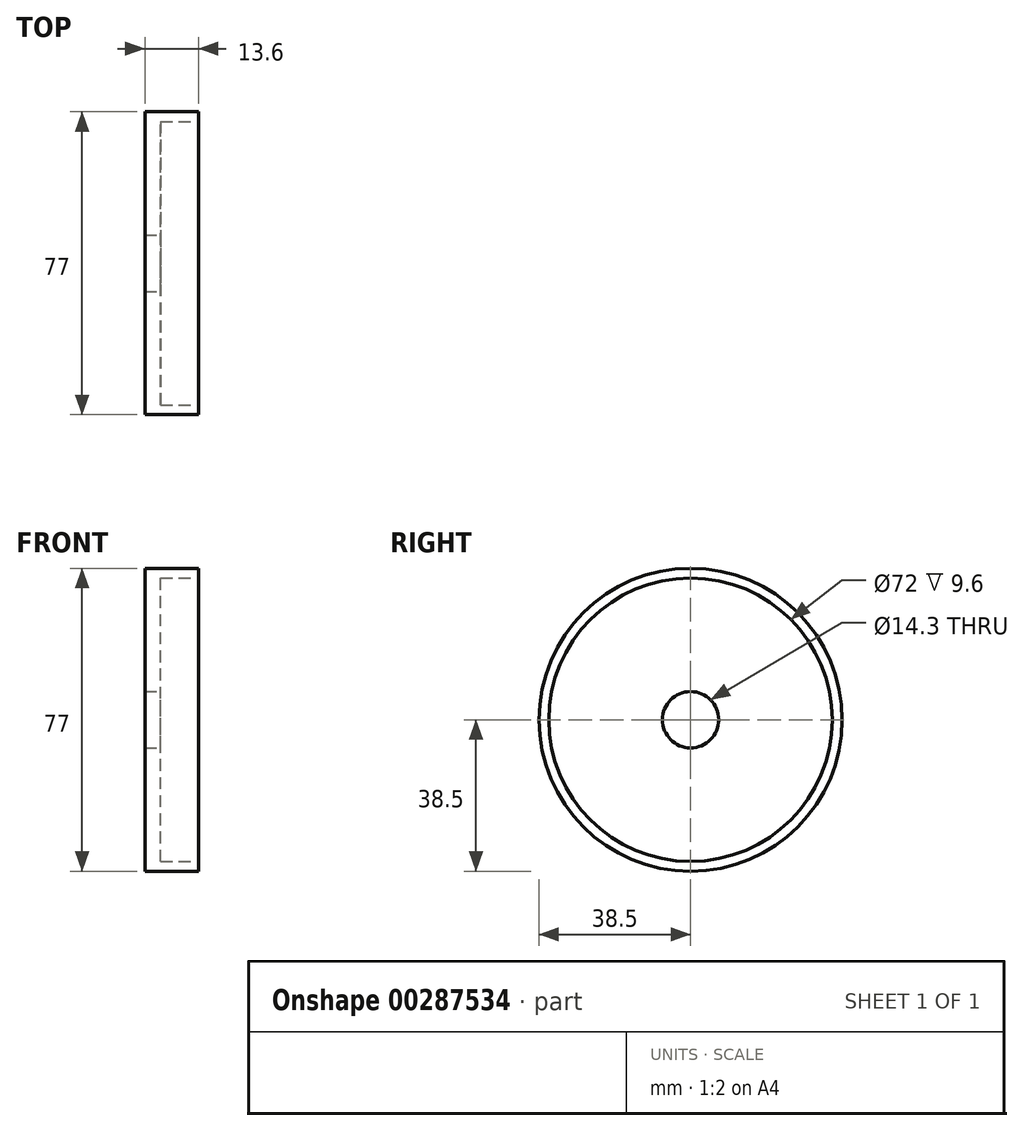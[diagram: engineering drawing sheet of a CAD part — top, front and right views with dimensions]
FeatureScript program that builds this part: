
annotation { "Feature Type Name" : "Feature", "Feature Type Description" : "" }
export const myFeature = defineFeature(function(context is Context, id is Id, definition is map)
    precondition{}
    {
        {
            var Q0;
            Q0=qCreatedBy(makeId("Front.planeOp"),FACE);
            var sketch = newSketch(context, id + "F0", { "sketchPlane" : qUnion([Q0])});
            skLineSegment(sketch, "E0", {"start": v(0, 0) * mm, "end": v(0, 36) * mm});
            skLineSegment(sketch, "E1", {"start": v(0, 36) * mm, "end": v(13.6, 36) * mm});
            skLineSegment(sketch, "E2", {"start": v(4, 0) * mm, "end": v(0, 0) * mm});
            skPoint(sketch, "E3", {"position": v(0, 7.15) * mm});
            skLineSegment(sketch, "E4", {"start": v(13.6, 36) * mm, "end": v(13.6, 38.5) * mm});
            skLineSegment(sketch, "E5", {"start": v(13.6, 38.5) * mm, "end": v(4, 38.5) * mm});
            skLineSegment(sketch, "E6", {"start": v(0, 36) * mm, "end": v(0, 38.5) * mm});
            skLineSegment(sketch, "E7", {"start": v(0, 38.5) * mm, "end": v(4, 38.5) * mm});
            skLineSegment(sketch, "E8", {"start": v(4, 0) * mm, "end": v(4, 36) * mm});
            skLineSegment(sketch, "E9", {"start": v(0, 7.15) * mm, "end": v(4, 7.15) * mm});
            skSolve(sketch);
        }
        {
            var Q0;
            {var subQ1=sQuery(id+"F0.wireOp",EDGE,"E1");Q0=makeQuery(id+"F0.imprint","IMPRINT",FACE,{"disambiguationData":[TD([[makeQuery(id+"F0.imprint","IMPRINT",EDGE,{"derivedFrom":subQ1}),-1.0]])]});}
            var Q1;
            {var subQ0=sQuery(id+"F0.wireOp",EDGE,"E4");Q1=makeQuery(id+"F0.imprint","IMPRINT",FACE,{"disambiguationData":[TD([[makeQuery(id+"F0.imprint","IMPRINT",EDGE,{"derivedFrom":subQ0}),1.0]])]});}
            var Q2;
            Q2=sQuery(id+"F0.wireOp",EDGE,"E2");
            revolve(context, id + "F1", {"entities" : qUnion([Q0, Q1]), "axis" : qUnion([Q2]), "revolveType" : RevolveType.FULL});
        }
    });
